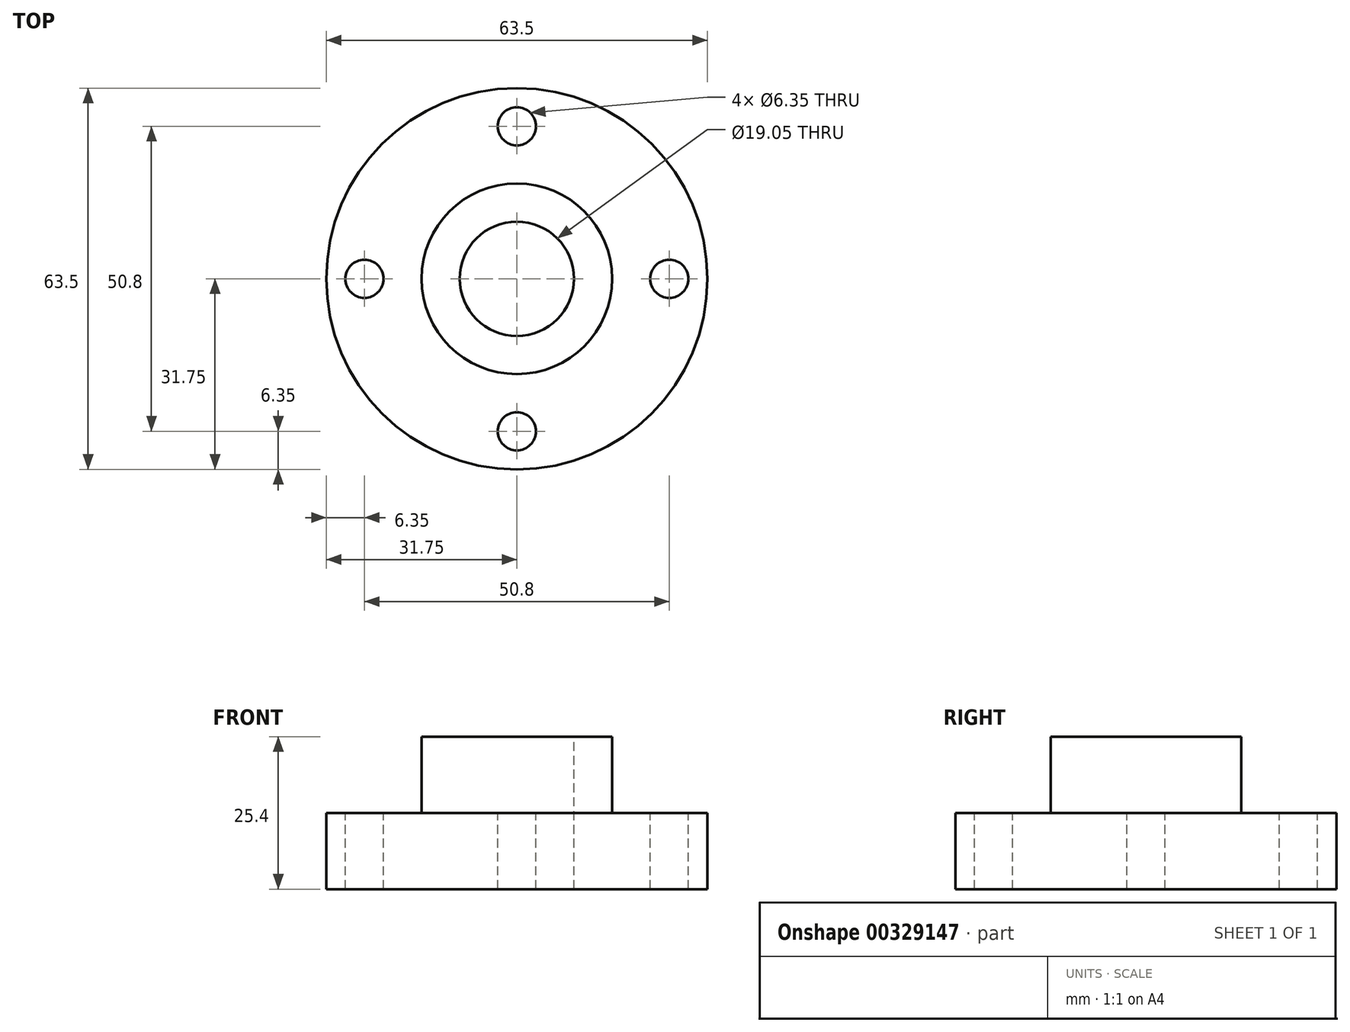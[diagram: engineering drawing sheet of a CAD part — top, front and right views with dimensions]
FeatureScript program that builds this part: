
annotation { "Feature Type Name" : "Feature", "Feature Type Description" : "" }
export const myFeature = defineFeature(function(context is Context, id is Id, definition is map)
    precondition{}
    {
        {
            var Q0;
            Q0=qCreatedBy(makeId("Top.planeOp"),FACE);
            var sketch = newSketch(context, id + "F0", { "sketchPlane" : qUnion([Q0])});
            skCircle(sketch, "E0", {"center": v(0, 0) * mm, "radius": 31.75 * mm});
            skSolve(sketch);
        }
        {
            var Q0;
            Q0 = qSketchRegion(id + "F0", true);
            extrude(context, id + "F1", {"entities" : qUnion([Q0]), "oppositeDirection" : true, "depth" : 12.7 * mm});
        }
        {
            var Q0;
            Q0=makeQuery(id+"F1.opExtrude","CAP_FACE",FACE,{"disambiguationData":[OSD([sQuery(id+"F0.wireOp",EDGE,"E0")])],"isStart":true});
            var sketch = newSketch(context, id + "F2", { "sketchPlane" : qUnion([Q0])});
            skCircle(sketch, "E1", {"center": v(0, 0) * mm, "radius": 15.88 * mm});
            skSolve(sketch);
        }
        {
            var Q0;
            Q0 = qSketchRegion(id + "F2", true);
            extrude(context, id + "F3", {"entities" : qUnion([Q0]), "operationType" : NewBodyOperationType.ADD, "depth" : 12.7 * mm});
        }
        {
            var Q0;
            Q0=makeQuery(id+"F3.opExtrude","CAP_FACE",FACE,{"disambiguationData":[OSD([sQuery(id+"F2.wireOp",EDGE,"E1")])],"isStart":false});
            var sketch = newSketch(context, id + "F4", { "sketchPlane" : qUnion([Q0])});
            skCircle(sketch, "E2", {"center": v(0, 0) * mm, "radius": 9.53 * mm});
            skSolve(sketch);
        }
        {
            var Q0;
            Q0 = qSketchRegion(id + "F4", true);
            extrude(context, id + "F5", {"entities" : qUnion([Q0]), "operationType" : NewBodyOperationType.REMOVE, "endBound" : BoundingType.THROUGH_ALL, "oppositeDirection" : true, "depth" : 25.4 * mm});
        }
        {
            var Q0;
            Q0=makeQuery(id+"F1.opExtrude","CAP_FACE",FACE,{"disambiguationData":[OSD([sQuery(id+"F0.wireOp",EDGE,"E0")])],"isStart":true});
            var sketch = newSketch(context, id + "F6", { "sketchPlane" : qUnion([Q0])});
            skCircle(sketch, "E3", {"center": v(0, 25.4) * mm, "radius": 3.18 * mm});
            skCircle(sketch, "E4", {"center": v(25.4, 0) * mm, "radius": 3.18 * mm});
            skCircle(sketch, "E5", {"center": v(0, -25.4) * mm, "radius": 3.18 * mm});
            skCircle(sketch, "E6", {"center": v(-25.4, 0) * mm, "radius": 3.18 * mm});
            skSolve(sketch);
        }
        {
            var Q0;
            Q0 = qSketchRegion(id + "F6", true);
            extrude(context, id + "F7", {"entities" : qUnion([Q0]), "operationType" : NewBodyOperationType.REMOVE, "endBound" : BoundingType.THROUGH_ALL, "oppositeDirection" : true, "depth" : 25.4 * mm});
        }
    });
